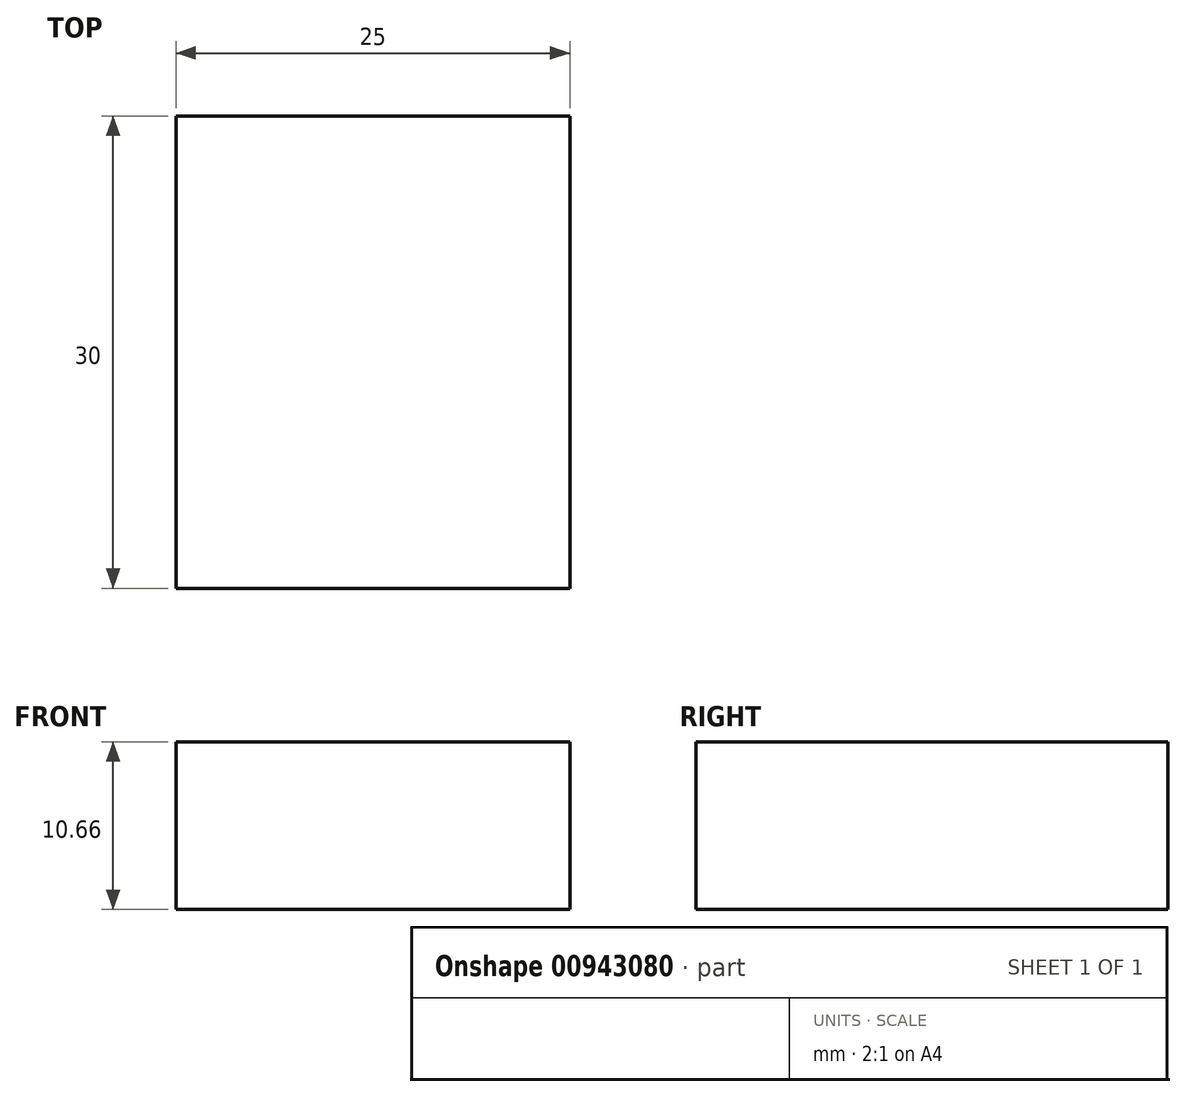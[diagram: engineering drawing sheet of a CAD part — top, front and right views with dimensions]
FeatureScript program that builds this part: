
annotation { "Feature Type Name" : "Feature", "Feature Type Description" : "" }
export const myFeature = defineFeature(function(context is Context, id is Id, definition is map)
    precondition{}
    {
        {
            var Q0;
            Q0=qCreatedBy(makeId("Right.planeOp"),FACE);
            var sketch = newSketch(context, id + "F0", { "sketchPlane" : qUnion([Q0])});
            skLineSegment(sketch, "E0.bottom", {"start": v(-36.58, 43.64) * mm, "end": v(-6.58, 43.64) * mm});
            skLineSegment(sketch, "E0.top", {"start": v(-36.58, 32.98) * mm, "end": v(-6.58, 32.98) * mm});
            skLineSegment(sketch, "E0.left", {"start": v(-36.58, 43.64) * mm, "end": v(-36.58, 32.98) * mm});
            skLineSegment(sketch, "E0.right", {"start": v(-6.58, 43.64) * mm, "end": v(-6.58, 32.98) * mm});
            skLineSegment(sketch, "E1.bottom", {"start": v(-26.58, 32.98) * mm, "end": v(-16.58, 32.98) * mm});
            skLineSegment(sketch, "E1.top", {"start": v(-26.58, 7.98) * mm, "end": v(-16.58, 7.98) * mm});
            skLineSegment(sketch, "E1.left", {"start": v(-26.58, 32.98) * mm, "end": v(-26.58, 7.98) * mm});
            skLineSegment(sketch, "E1.right", {"start": v(-16.58, 32.98) * mm, "end": v(-16.58, 7.98) * mm});
            skSolve(sketch);
        }
        {
            var Q0;
            Q0=makeQuery(id+"F0.imprint","IMPRINT",FACE,{"disambiguationData":[TD([[makeQuery(id+"F0.imprint","IMPRINT",EDGE,{"derivedFrom":sQuery(id+"F0.wireOp",EDGE,"E0.bottom")}),-1.0]])]});
            var Q1;
            Q1=makeQuery(id+"F0.imprint","IMPRINT",FACE,{"disambiguationData":[TD([[makeQuery(id+"F0.imprint","IMPRINT",EDGE,{"derivedFrom":sQuery(id+"F0.wireOp",EDGE,"E1.bottom")}),-1.0]])]});
            extrude(context, id + "F1", {"entities" : qUnion([Q0, Q1]), "depth" : 15 * mm, "offsetDistance" : 25 * mm});
        }
        {
            var Q0;
            Q0=makeQuery(id+"F1.opExtrude","CAP_FACE",FACE,{"disambiguationData":[OSD([sQuery(id+"F0.wireOp",EDGE,"E0.bottom"),sQuery(id+"F0.wireOp",EDGE,"E0.top"),sQuery(id+"F0.wireOp",EDGE,"E0.left"),sQuery(id+"F0.wireOp",EDGE,"E0.right"),sQuery(id+"F0.wireOp",EDGE,"E1.top"),sQuery(id+"F0.wireOp",EDGE,"E1.left"),sQuery(id+"F0.wireOp",EDGE,"E1.right")])],"isStart":false});
            var sketch = newSketch(context, id + "F2", { "sketchPlane" : qUnion([Q0])});
            skLineSegment(sketch, "E2.bottom", {"start": v(-36.58, 43.64) * mm, "end": v(-6.58, 43.64) * mm});
            skLineSegment(sketch, "E2.top", {"start": v(-36.58, 32.98) * mm, "end": v(-6.58, 32.98) * mm});
            skLineSegment(sketch, "E2.left", {"start": v(-36.58, 43.64) * mm, "end": v(-36.58, 32.98) * mm});
            skLineSegment(sketch, "E2.right", {"start": v(-6.58, 43.64) * mm, "end": v(-6.58, 32.98) * mm});
            skSolve(sketch);
        }
        {
            var Q0;
            Q0=makeQuery(id+"F2.imprint","IMPRINT",FACE,{"disambiguationData":[TD([[makeQuery(id+"F2.imprint","IMPRINT",EDGE,{"derivedFrom":sQuery(id+"F2.wireOp",EDGE,"E2.bottom")}),-1.0]])]});
            extrude(context, id + "F3", {"entities" : qUnion([Q0]), "operationType" : NewBodyOperationType.ADD, "depth" : 10 * mm, "offsetDistance" : 25 * mm});
        }
    });
